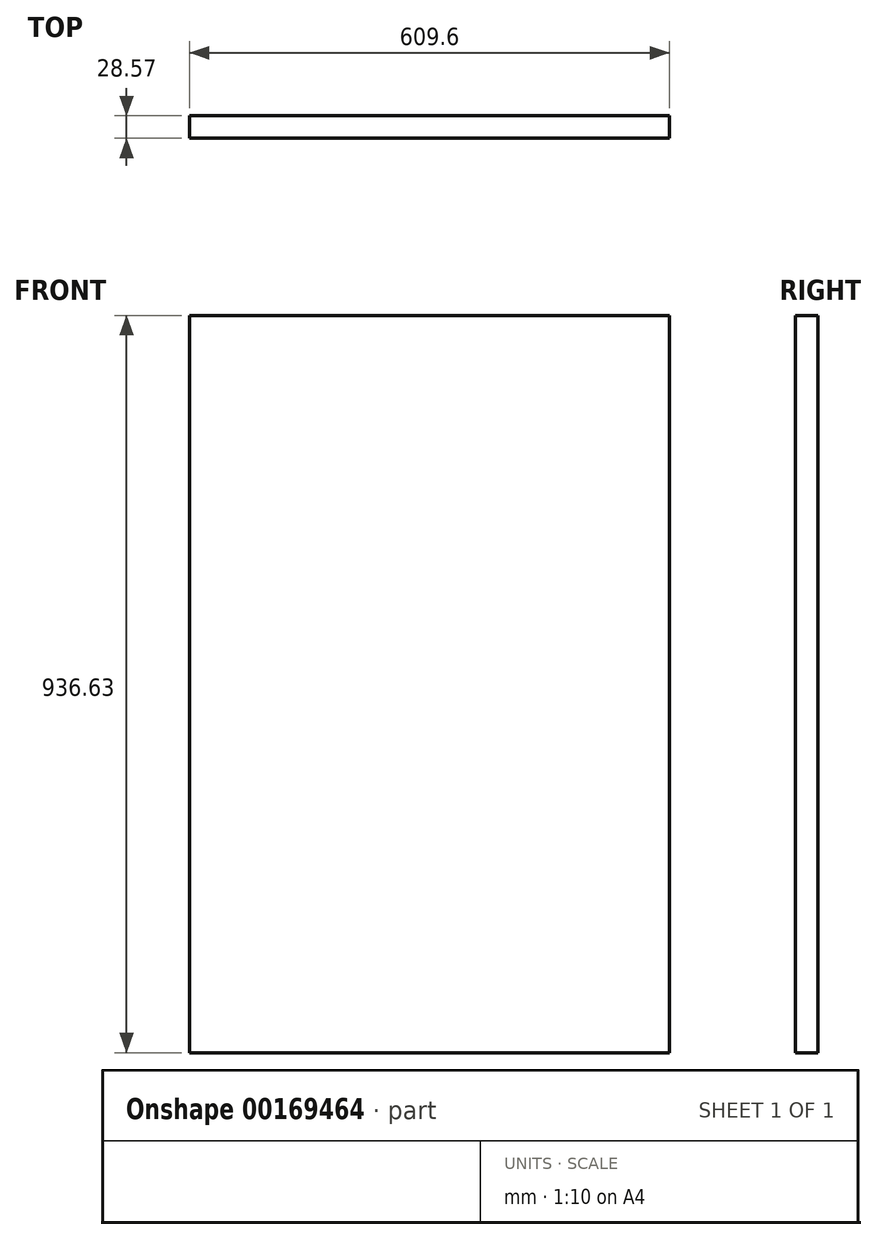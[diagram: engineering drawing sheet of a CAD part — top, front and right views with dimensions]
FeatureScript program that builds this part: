
annotation { "Feature Type Name" : "Feature", "Feature Type Description" : "" }
export const myFeature = defineFeature(function(context is Context, id is Id, definition is map)
    precondition{}
    {
        {
            var Q0;
            Q0=qCreatedBy(makeId("Front.planeOp"),FACE);
            var sketch = newSketch(context, id + "F0", { "sketchPlane" : qUnion([Q0])});
            skLineSegment(sketch, "E0.bottom", {"start": v(-307.89, 577.42) * mm, "end": v(301.71, 577.42) * mm});
            skLineSegment(sketch, "E0.top", {"start": v(-307.89, -359.2) * mm, "end": v(301.71, -359.2) * mm});
            skLineSegment(sketch, "E0.left", {"start": v(-307.89, 577.42) * mm, "end": v(-307.89, -359.2) * mm});
            skLineSegment(sketch, "E0.right", {"start": v(301.71, 577.42) * mm, "end": v(301.71, -359.2) * mm});
            skSolve(sketch);
        }
        {
            var Q0;
            Q0 = qSketchRegion(id + "F0", true);
            extrude(context, id + "F1", {"entities" : qUnion([Q0]), "depth" : 28.57 * mm});
        }
    });
